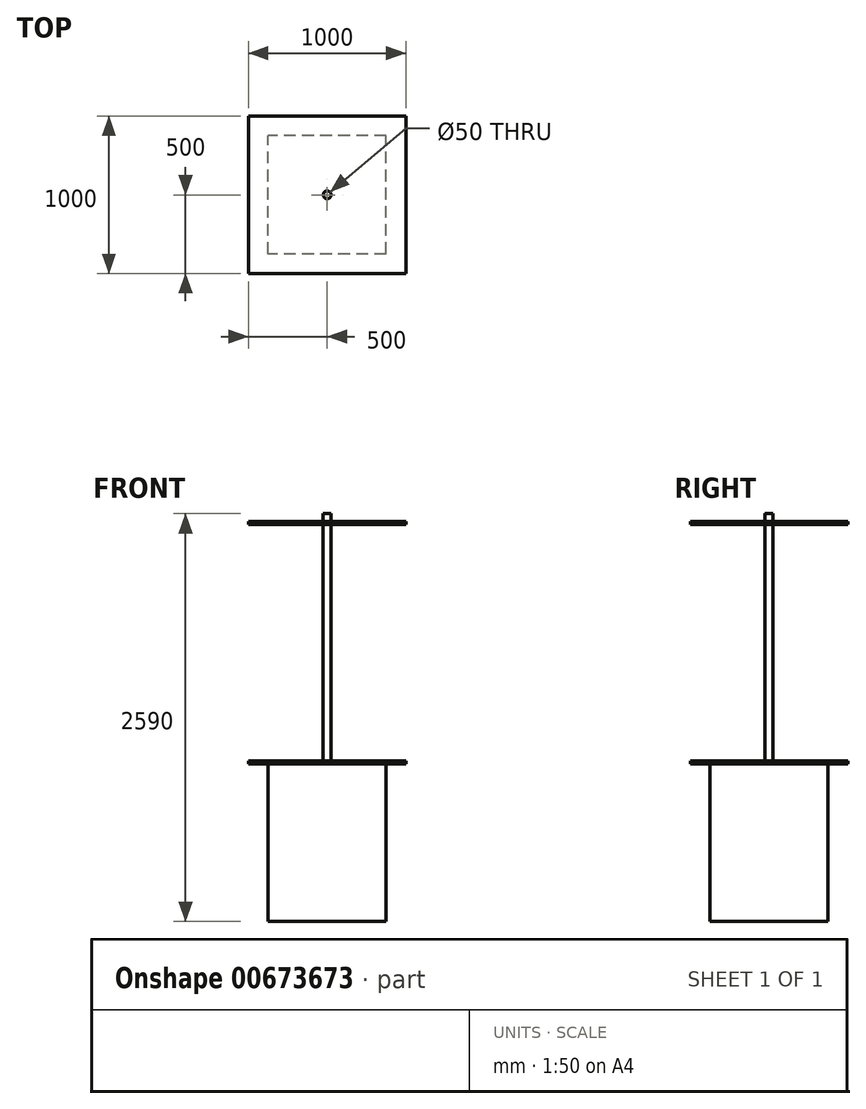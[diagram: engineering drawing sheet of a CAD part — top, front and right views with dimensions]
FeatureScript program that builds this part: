
annotation { "Feature Type Name" : "Feature", "Feature Type Description" : "" }
export const myFeature = defineFeature(function(context is Context, id is Id, definition is map)
    precondition{}
    {
        {
            var Q0;
            Q0=qCreatedBy(makeId("Top.planeOp"),FACE);
            var sketch = newSketch(context, id + "F0", { "sketchPlane" : qUnion([Q0])});
            skLineSegment(sketch, "E0.bottom", {"start": v(375, -375) * mm, "end": v(-375, -375) * mm});
            skLineSegment(sketch, "E0.top", {"start": v(375, 375) * mm, "end": v(-375, 375) * mm});
            skLineSegment(sketch, "E0.left", {"start": v(375, -375) * mm, "end": v(375, 375) * mm});
            skLineSegment(sketch, "E0.right", {"start": v(-375, -375) * mm, "end": v(-375, 375) * mm});
            skPoint(sketch, "E0.middle", {"position": v(0, 0) * mm});
            skSolve(sketch);
        }
        {
            var Q0;
            Q0=makeQuery(id+"F0.imprint","IMPRINT",FACE,{"disambiguationData":[TD([[makeQuery(id+"F0.imprint","IMPRINT",EDGE,{"derivedFrom":sQuery(id+"F0.wireOp",EDGE,"E0.bottom")}),-1.0]])]});
            extrude(context, id + "F1", {"entities" : qUnion([Q0]), "depth" : 1000 * mm, "offsetDistance" : 25 * mm});
        }
        {
            var Q0;
            Q0=makeQuery(id+"F1.opExtrude","CAP_FACE",FACE,{"disambiguationData":[OSD([sQuery(id+"F0.wireOp",EDGE,"E0.bottom"),sQuery(id+"F0.wireOp",EDGE,"E0.top"),sQuery(id+"F0.wireOp",EDGE,"E0.left"),sQuery(id+"F0.wireOp",EDGE,"E0.right")])],"isStart":false});
            var sketch = newSketch(context, id + "F2", { "sketchPlane" : qUnion([Q0])});
            skLineSegment(sketch, "E1.bottom", {"start": v(500, -500) * mm, "end": v(-500, -500) * mm});
            skLineSegment(sketch, "E1.top", {"start": v(500, 500) * mm, "end": v(-500, 500) * mm});
            skLineSegment(sketch, "E1.left", {"start": v(500, -500) * mm, "end": v(500, 500) * mm});
            skLineSegment(sketch, "E1.right", {"start": v(-500, -500) * mm, "end": v(-500, 500) * mm});
            skPoint(sketch, "E1.middle", {"position": v(0, 0) * mm});
            skSolve(sketch);
        }
        {
            var Q0;
            Q0=makeQuery(id+"F2.imprint","IMPRINT",FACE,{"disambiguationData":[TD([[makeQuery(id+"F2.imprint","IMPRINT",EDGE,{"derivedFrom":sQuery(id+"F2.wireOp",EDGE,"E1.bottom")}),-1.0]])]});
            var Q1;
            Q1=makeQuery(id+"F2.imprint","IMPRINT",FACE,{"disambiguationData":[TD([[makeQuery(id+"F2.imprint","IMPRINT",EDGE,{"derivedFrom":makeQuery(id+"F1.opExtrude","CAP_EDGE",EDGE,{"disambiguationData":[OSD([sQuery(id+"F0.wireOp",EDGE,"E0.bottom")])],"isStart":false})}),-1.0]])]});
            var Q2;
            Q2 = qSketchRegion(id + "F2", true);
            extrude(context, id + "F3", {"entities" : qUnion([Q0, Q1, Q2]), "operationType" : NewBodyOperationType.ADD, "depth" : 20 * mm, "offsetDistance" : 25 * mm});
        }
        {
            var Q0;
            Q0=makeQuery(id+"F3.opExtrude","CAP_FACE",FACE,{"disambiguationData":[OSD([sQuery(id+"F2.wireOp",EDGE,"E1.bottom"),sQuery(id+"F2.wireOp",EDGE,"E1.top"),sQuery(id+"F2.wireOp",EDGE,"E1.left"),sQuery(id+"F2.wireOp",EDGE,"E1.right")])],"isStart":false});
            var sketch = newSketch(context, id + "F4", { "sketchPlane" : qUnion([Q0])});
            skCircle(sketch, "E2", {"center": v(0, 0) * mm, "radius": 25 * mm});
            skSolve(sketch);
        }
        {
            var Q0;
            Q0=makeQuery(id+"F4.imprint","IMPRINT",FACE,{"disambiguationData":[TD([[makeQuery(id+"F4.imprint","IMPRINT",EDGE,{"derivedFrom":sQuery(id+"F4.wireOp",EDGE,"E2")}),1.0]])]});
            extrude(context, id + "F5", {"entities" : qUnion([Q0]), "operationType" : NewBodyOperationType.ADD, "depth" : 1500 * mm, "offsetDistance" : 25 * mm});
        }
        {
            var Q0;
            Q0=makeQuery(id+"F5.opExtrude","CAP_FACE",FACE,{"disambiguationData":[OSD([sQuery(id+"F4.wireOp",EDGE,"E2")])],"isStart":false});
            var sketch = newSketch(context, id + "F6", { "sketchPlane" : qUnion([Q0])});
            skLineSegment(sketch, "E3.bottom", {"start": v(500, -500) * mm, "end": v(-500, -500) * mm});
            skLineSegment(sketch, "E3.top", {"start": v(500, 500) * mm, "end": v(-500, 500) * mm});
            skLineSegment(sketch, "E3.left", {"start": v(500, -500) * mm, "end": v(500, 500) * mm});
            skLineSegment(sketch, "E3.right", {"start": v(-500, -500) * mm, "end": v(-500, 500) * mm});
            skPoint(sketch, "E3.middle", {"position": v(0, 0) * mm});
            skSolve(sketch);
        }
        {
            var Q0;
            Q0=makeQuery(id+"F6.imprint","IMPRINT",FACE,{"disambiguationData":[TD([[makeQuery(id+"F6.imprint","IMPRINT",EDGE,{"derivedFrom":sQuery(id+"F6.wireOp",EDGE,"E3.bottom")}),-1.0]])]});
            extrude(context, id + "F7", {"entities" : qUnion([Q0]), "depth" : 20 * mm, "offsetDistance" : 25 * mm});
        }
        {
            var Q0;
            Q0=makeQuery(id+"F5.opExtrude","CAP_FACE",FACE,{"disambiguationData":[OSD([sQuery(id+"F4.wireOp",EDGE,"E2")])],"isStart":false});
            var sketch = newSketch(context, id + "F8", { "sketchPlane" : qUnion([Q0])});
            skCircle(sketch, "E4", {"center": v(0, 0) * mm, "radius": 25 * mm});
            skSolve(sketch);
        }
        {
            var Q0;
            Q0=makeQuery(id+"F8.imprint","IMPRINT",FACE,{"disambiguationData":[TD([[makeQuery(id+"F8.imprint","IMPRINT",EDGE,{"derivedFrom":sQuery(id+"F8.wireOp",EDGE,"E4")}),1.0]])]});
            extrude(context, id + "F9", {"entities" : qUnion([Q0]), "depth" : 70 * mm, "offsetDistance" : 25 * mm});
        }
    });
